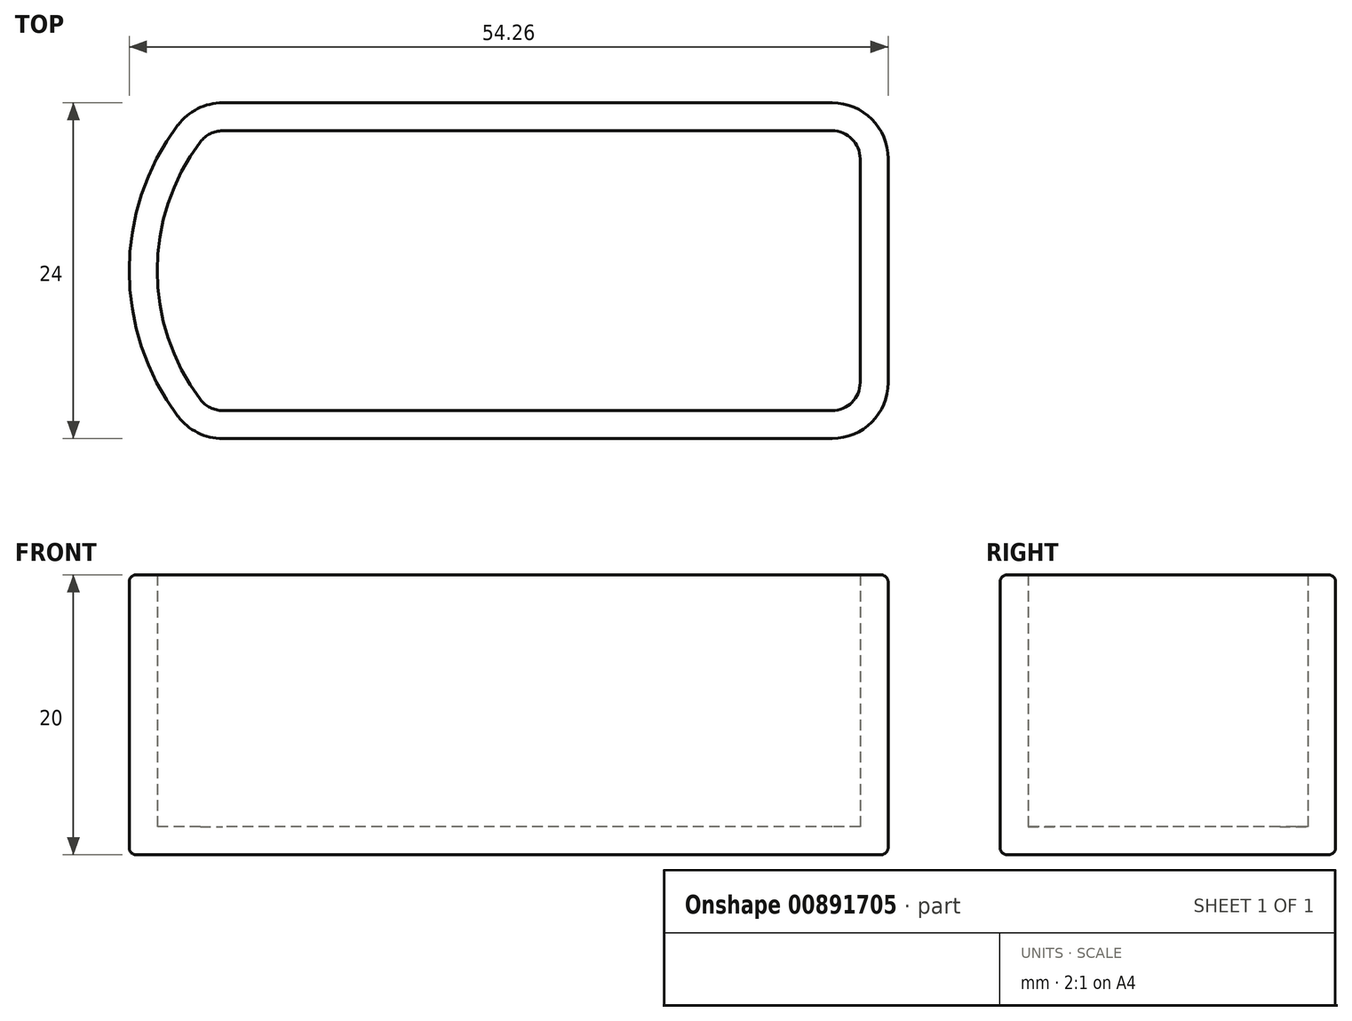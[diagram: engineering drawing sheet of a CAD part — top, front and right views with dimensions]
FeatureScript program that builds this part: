
annotation { "Feature Type Name" : "Feature", "Feature Type Description" : "" }
export const myFeature = defineFeature(function(context is Context, id is Id, definition is map)
    precondition{}
    {
        {
            var Q0;
            Q0=qCreatedBy(makeId("Top.planeOp"),FACE);
            var sketch = newSketch(context, id + "F0", { "sketchPlane" : qUnion([Q0])});
            skLineSegment(sketch, "E0.bottom", {"start": v(23.9, 6.76) * mm, "end": v(-19.68, 6.76) * mm});
            skLineSegment(sketch, "E0.top", {"start": v(23.9, -13.24) * mm, "end": v(-19.68, -13.24) * mm});
            skLineSegment(sketch, "E0.left", {"start": v(25.9, 4.76) * mm, "end": v(25.9, -11.24) * mm});
            skPoint(sketch, "E1.visualSharp", {"position": v(25.9, 6.76) * mm});
            skArc(sketch, "E1.filletArc", {"start": v(25.9, 4.76) * mm, "mid": v(25.32, 6.17) * mm, "end": v(23.9, 6.76) * mm});
            skPoint(sketch, "E2.visualSharp", {"position": v(25.9, -13.24) * mm});
            skArc(sketch, "E2.filletArc", {"start": v(23.9, -13.24) * mm, "mid": v(25.32, -12.66) * mm, "end": v(25.9, -11.24) * mm});
            skArc(sketch, "E3", {"start": v(-21.28, 5.96) * mm, "mid": v(-24.36, -3.24) * mm, "end": v(-21.28, -12.45) * mm});
            skPoint(sketch, "E4.visualSharp", {"position": v(-20.64, 6.76) * mm});
            skArc(sketch, "E4.filletArc", {"start": v(-19.68, 6.76) * mm, "mid": v(-20.57, 6.55) * mm, "end": v(-21.28, 5.96) * mm});
            skPoint(sketch, "E5.visualSharp", {"position": v(-20.64, -13.24) * mm});
            skArc(sketch, "E5.filletArc", {"start": v(-21.28, -12.45) * mm, "mid": v(-20.57, -13.03) * mm, "end": v(-19.68, -13.24) * mm});
            skArc(sketch, "E6.0", {"start": v(27.9, 4.76) * mm, "mid": v(26.73, 7.59) * mm, "end": v(23.9, 8.76) * mm});
            skLineSegment(sketch, "E6.1", {"start": v(23.9, 8.76) * mm, "end": v(-19.68, 8.76) * mm});
            skLineSegment(sketch, "E6.2", {"start": v(27.9, 4.76) * mm, "end": v(27.9, -11.24) * mm});
            skArc(sketch, "E6.3", {"start": v(-19.68, 8.76) * mm, "mid": v(-21.47, 8.34) * mm, "end": v(-22.88, 7.17) * mm});
            skArc(sketch, "E6.4", {"start": v(23.9, -15.24) * mm, "mid": v(26.73, -14.07) * mm, "end": v(27.9, -11.24) * mm});
            skLineSegment(sketch, "E6.5", {"start": v(23.9, -15.24) * mm, "end": v(-19.68, -15.24) * mm});
            skArc(sketch, "E6.6", {"start": v(-22.88, -13.65) * mm, "mid": v(-21.47, -14.82) * mm, "end": v(-19.68, -15.24) * mm});
            skArc(sketch, "E6.7", {"start": v(-22.88, 7.17) * mm, "mid": v(-26.36, -3.24) * mm, "end": v(-22.88, -13.65) * mm});
            skSolve(sketch);
        }
        {
            var Q0;
            Q0=makeQuery(id+"F0.imprint","IMPRINT",FACE,{"disambiguationData":[TD([[makeQuery(id+"F0.imprint","IMPRINT",EDGE,{"derivedFrom":sQuery(id+"F0.wireOp",EDGE,"E0.bottom")}),1.0]])]});
            extrude(context, id + "F1", {"entities" : qUnion([Q0]), "depth" : 2 * mm, "offsetDistance" : 25 * mm});
        }
        {
            var Q0;
            Q0=makeQuery(id+"F0.imprint","IMPRINT",FACE,{"disambiguationData":[TD([[makeQuery(id+"F0.imprint","IMPRINT",EDGE,{"derivedFrom":sQuery(id+"F0.wireOp",EDGE,"E0.bottom")}),-1.0]])]});
            extrude(context, id + "F2", {"entities" : qUnion([Q0]), "operationType" : NewBodyOperationType.ADD, "depth" : 20 * mm, "offsetDistance" : 25 * mm});
        }
        {
            var Q0;
            Q0=makeQuery(id+"F2.opExtrude","CAP_EDGE",EDGE,{"disambiguationData":[OSD([sQuery(id+"F0.wireOp",EDGE,"E6.5")])],"isStart":true});
            fillet(context, id + "F3", {"entities" : qUnion([Q0]), "radius" : 0.5 * mm, "tangentPropagation" : true, "allowEdgeOverflow" : false});
        }
        {
            var Q0;
            Q0=makeQuery(id+"F2.opExtrude","CAP_EDGE",EDGE,{"disambiguationData":[OSD([sQuery(id+"F0.wireOp",EDGE,"E6.5")])],"isStart":false});
            fillet(context, id + "F4", {"entities" : qUnion([Q0]), "radius" : 0.5 * mm, "tangentPropagation" : true, "allowEdgeOverflow" : false});
        }
    });
